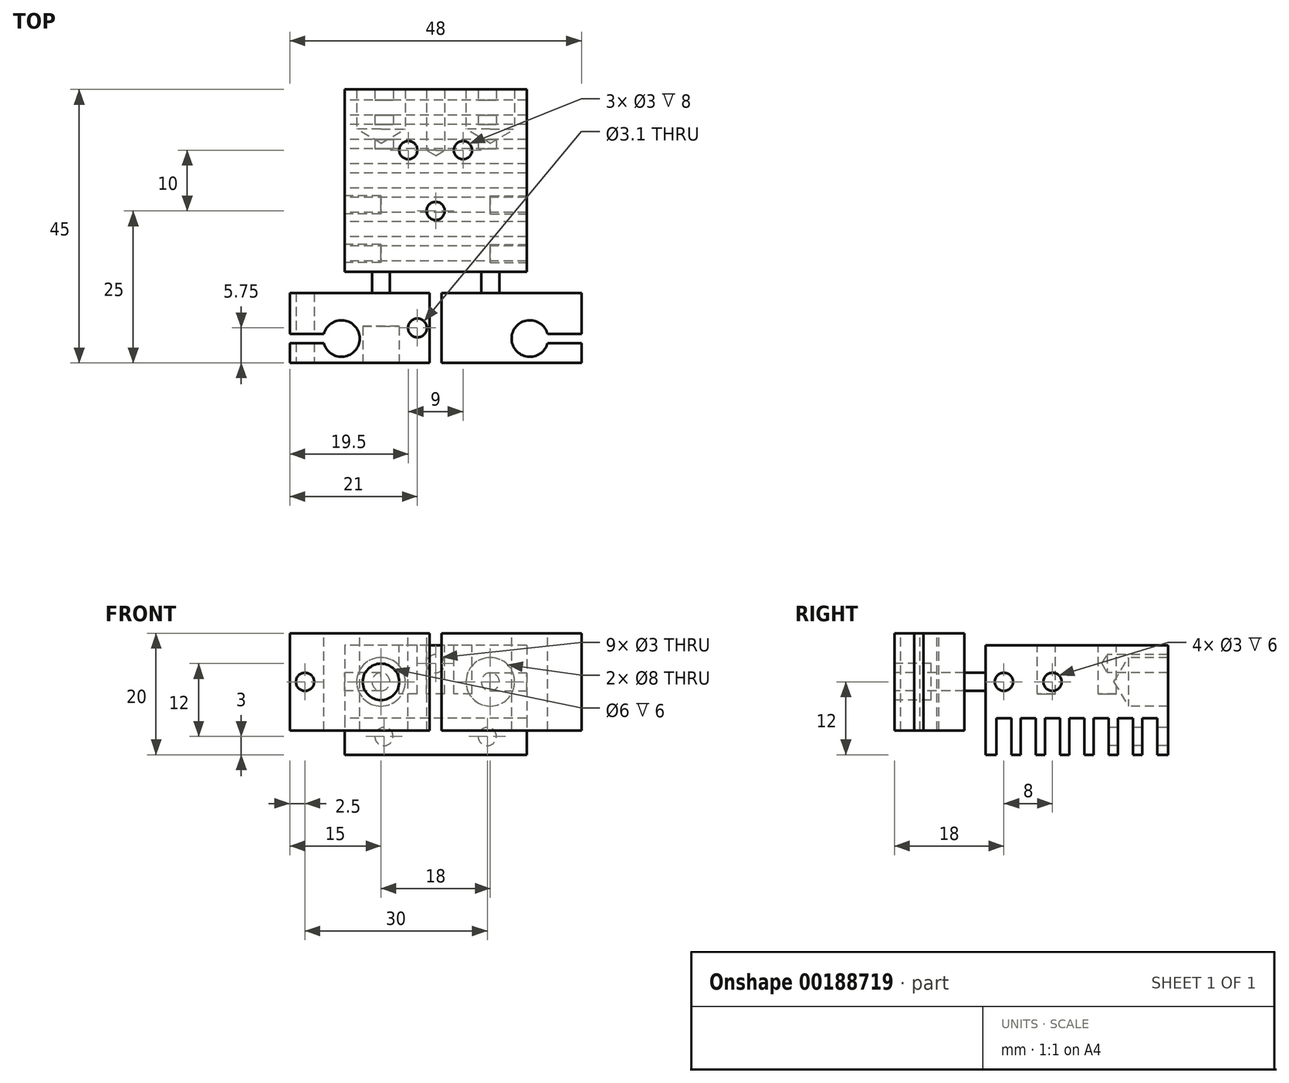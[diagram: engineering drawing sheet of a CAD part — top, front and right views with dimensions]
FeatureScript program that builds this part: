
annotation { "Feature Type Name" : "Feature", "Feature Type Description" : "" }
export const myFeature = defineFeature(function(context is Context, id is Id, definition is map)
    precondition{}
    {
        {
            var Q0;
            Q0=qCreatedBy(makeId("Top.planeOp"),FACE);
            var sketch = newSketch(context, id + "F0", { "sketchPlane" : qUnion([Q0])});
            skLineSegment(sketch, "E0.bottom", {"start": v(15, -15) * mm, "end": v(-15, -15) * mm});
            skLineSegment(sketch, "E0.top", {"start": v(15, 15) * mm, "end": v(-15, 15) * mm});
            skLineSegment(sketch, "E0.left", {"start": v(15, -15) * mm, "end": v(15, 15) * mm});
            skLineSegment(sketch, "E0.right", {"start": v(-15, -15) * mm, "end": v(-15, 15) * mm});
            skPoint(sketch, "E0.middle", {"position": v(0, 0) * mm});
            skSolve(sketch);
        }
        {
            var Q0;
            Q0=makeQuery(id+"F0.imprint","IMPRINT",FACE,{"disambiguationData":[TD([[makeQuery(id+"F0.imprint","IMPRINT",EDGE,{"derivedFrom":sQuery(id+"F0.wireOp",EDGE,"E0.bottom")}),-1.0]])]});
            extrude(context, id + "F15", {"entities" : qUnion([Q0]), "depth" : 18 * mm});
        }
        {
            var Q0;
            Q0=makeQuery(id+"F15.opExtrude","SWEPT_FACE",FACE,{"disambiguationData":[OSD([sQuery(id+"F0.wireOp",EDGE,"E0.top")])]});
            var sketch = newSketch(context, id + "F16", { "sketchPlane" : qUnion([Q0])});
            skPoint(sketch, "E1", {"position": v(-8.5, 3) * mm});
            skPoint(sketch, "E2", {"position": v(8.5, 3) * mm});
            skPoint(sketch, "E3", {"position": v(-9, 12) * mm});
            skPoint(sketch, "E4", {"position": v(9, 12) * mm});
            skPoint(sketch, "E5", {"position": v(0, 15) * mm});
            skSolve(sketch);
        }
        {
            var Q0;
            Q0=sQuery(id+"F16.wireOp",VERTEX,"E3");
            var Q1;
            Q1=sQuery(id+"F16.wireOp",VERTEX,"E4");
            var Q2;
            Q2=makeQuery(id+"F15.opExtrude","SWEPT_BODY",BODY,{"disambiguationData":[OSD([sQuery(id+"F0.wireOp",EDGE,"E0.bottom"),sQuery(id+"F0.wireOp",EDGE,"E0.top"),sQuery(id+"F0.wireOp",EDGE,"E0.left"),sQuery(id+"F0.wireOp",EDGE,"E0.right")])]});
            hole(context, id + "F1", {"style" : HoleStyle.SIMPLE, "endStyle" : HoleEndStyle.BLIND, "holeDiameter" : 8 * mm, "holeDepth" : 6.5 * mm, "locations" : qUnion([Q0, Q1]), "scope" : qUnion([Q2]), "tappedDepth" : 12 * mm, "tapClearance" : 3, "startStyle" : HoleStartStyle.PART});
        }
        {
            var Q0;
            Q0=makeQuery(id+"F15.opExtrude","CAP_FACE",FACE,{"disambiguationData":[OSD([sQuery(id+"F0.wireOp",EDGE,"E0.bottom"),sQuery(id+"F0.wireOp",EDGE,"E0.top"),sQuery(id+"F0.wireOp",EDGE,"E0.left"),sQuery(id+"F0.wireOp",EDGE,"E0.right")])],"isStart":true});
            var sketch = newSketch(context, id + "F17", { "sketchPlane" : qUnion([Q0])});
            skLineSegment(sketch, "E6.bottom", {"start": v(15, -13.25) * mm, "end": v(-15.01, -13.25) * mm});
            skLineSegment(sketch, "E6.top", {"start": v(15, -10.75) * mm, "end": v(-15.01, -10.75) * mm});
            skLineSegment(sketch, "E6.left", {"start": v(15, -13.25) * mm, "end": v(15, -10.75) * mm});
            skLineSegment(sketch, "E6.right", {"start": v(-15.01, -13.25) * mm, "end": v(-15.01, -10.75) * mm});
            skLineSegment(sketch, "E7.0.1.0", {"start": v(15, -9.25) * mm, "end": v(15, -6.75) * mm});
            skLineSegment(sketch, "E7.0.1.1", {"start": v(-15.01, -9.25) * mm, "end": v(-15.01, -6.75) * mm});
            skLineSegment(sketch, "E7.0.1.2", {"start": v(15, -9.25) * mm, "end": v(-15.01, -9.25) * mm});
            skLineSegment(sketch, "E7.0.1.3", {"start": v(15, -6.75) * mm, "end": v(-15.01, -6.75) * mm});
            skLineSegment(sketch, "E7.0.2.0", {"start": v(15, -5.25) * mm, "end": v(15, -2.75) * mm});
            skLineSegment(sketch, "E7.0.2.1", {"start": v(-15.01, -5.25) * mm, "end": v(-15.01, -2.75) * mm});
            skLineSegment(sketch, "E7.0.2.2", {"start": v(15, -5.25) * mm, "end": v(-15.01, -5.25) * mm});
            skLineSegment(sketch, "E7.0.2.3", {"start": v(15, -2.75) * mm, "end": v(-15.01, -2.75) * mm});
            skLineSegment(sketch, "E7.0.3.0", {"start": v(15, -1.25) * mm, "end": v(15, 1.25) * mm});
            skLineSegment(sketch, "E7.0.3.1", {"start": v(-15.01, -1.25) * mm, "end": v(-15.01, 1.25) * mm});
            skLineSegment(sketch, "E7.0.3.2", {"start": v(15, -1.25) * mm, "end": v(-15.01, -1.25) * mm});
            skLineSegment(sketch, "E7.0.3.3", {"start": v(15, 1.25) * mm, "end": v(-15.01, 1.25) * mm});
            skLineSegment(sketch, "E7.0.4.0", {"start": v(15, 2.75) * mm, "end": v(15, 5.25) * mm});
            skLineSegment(sketch, "E7.0.4.1", {"start": v(-15.01, 2.75) * mm, "end": v(-15.01, 5.25) * mm});
            skLineSegment(sketch, "E7.0.4.2", {"start": v(15, 2.75) * mm, "end": v(-15.01, 2.75) * mm});
            skLineSegment(sketch, "E7.0.4.3", {"start": v(15, 5.25) * mm, "end": v(-15.01, 5.25) * mm});
            skLineSegment(sketch, "E7.0.5.0", {"start": v(15, 6.75) * mm, "end": v(15, 9.25) * mm});
            skLineSegment(sketch, "E7.0.5.1", {"start": v(-15.01, 6.75) * mm, "end": v(-15.01, 9.25) * mm});
            skLineSegment(sketch, "E7.0.5.2", {"start": v(15, 6.75) * mm, "end": v(-15.01, 6.75) * mm});
            skLineSegment(sketch, "E7.0.5.3", {"start": v(15, 9.25) * mm, "end": v(-15.01, 9.25) * mm});
            skLineSegment(sketch, "E7.0.6.0", {"start": v(15, 10.75) * mm, "end": v(15, 13.25) * mm});
            skLineSegment(sketch, "E7.0.6.1", {"start": v(-15.01, 10.75) * mm, "end": v(-15.01, 13.25) * mm});
            skLineSegment(sketch, "E7.0.6.2", {"start": v(15, 10.75) * mm, "end": v(-15.01, 10.75) * mm});
            skLineSegment(sketch, "E7.0.6.3", {"start": v(15, 13.25) * mm, "end": v(-15.01, 13.25) * mm});
            skLineSegment(sketch, "E7.direction1", {"start": v(-15.01, -13.25) * mm, "end": v(9.99, -13.25) * mm, "construction": true});
            skLineSegment(sketch, "E7.direction2", {"start": v(-15.01, -13.25) * mm, "end": v(-15.01, -9.25) * mm, "construction": true});
            skSolve(sketch);
        }
        {
            var Q0;
            {var subQ0=sQuery(id+"F17.wireOp",EDGE,"E7.0.6.0");Q0=makeQuery(id+"F17.imprint","IMPRINT",FACE,{"disambiguationData":[TD([[makeQuery(id+"F17.imprint","IMPRINT",EDGE,{"derivedFrom":subQ0}),-1.0]])]});}
            var Q1;
            {var subQ0=sQuery(id+"F17.wireOp",EDGE,"E7.0.5.0");Q1=makeQuery(id+"F17.imprint","IMPRINT",FACE,{"disambiguationData":[TD([[makeQuery(id+"F17.imprint","IMPRINT",EDGE,{"derivedFrom":subQ0}),-1.0]])]});}
            var Q2;
            {var subQ0=sQuery(id+"F17.wireOp",EDGE,"E7.0.4.0");Q2=makeQuery(id+"F17.imprint","IMPRINT",FACE,{"disambiguationData":[TD([[makeQuery(id+"F17.imprint","IMPRINT",EDGE,{"derivedFrom":subQ0}),-1.0]])]});}
            var Q3;
            {var subQ0=sQuery(id+"F17.wireOp",EDGE,"E7.0.3.0");Q3=makeQuery(id+"F17.imprint","IMPRINT",FACE,{"disambiguationData":[TD([[makeQuery(id+"F17.imprint","IMPRINT",EDGE,{"derivedFrom":subQ0}),-1.0]])]});}
            var Q4;
            {var subQ0=sQuery(id+"F17.wireOp",EDGE,"E7.0.2.0");Q4=makeQuery(id+"F17.imprint","IMPRINT",FACE,{"disambiguationData":[TD([[makeQuery(id+"F17.imprint","IMPRINT",EDGE,{"derivedFrom":subQ0}),-1.0]])]});}
            var Q5;
            {var subQ0=sQuery(id+"F17.wireOp",EDGE,"E7.0.1.0");Q5=makeQuery(id+"F17.imprint","IMPRINT",FACE,{"disambiguationData":[TD([[makeQuery(id+"F17.imprint","IMPRINT",EDGE,{"derivedFrom":subQ0}),-1.0]])]});}
            var Q6;
            {var subQ0=sQuery(id+"F17.wireOp",EDGE,"E6.left");Q6=makeQuery(id+"F17.imprint","IMPRINT",FACE,{"disambiguationData":[TD([[makeQuery(id+"F17.imprint","IMPRINT",EDGE,{"derivedFrom":subQ0}),-1.0]])]});}
            extrude(context, id + "F18", {"entities" : qUnion([Q0, Q1, Q2, Q3, Q4, Q5, Q6]), "operationType" : NewBodyOperationType.REMOVE, "oppositeDirection" : true, "depth" : 6 * mm});
        }
        {
            var Q0;
            Q0=sQuery(id+"F16.wireOp",VERTEX,"E2");
            var Q1;
            Q1=sQuery(id+"F16.wireOp",VERTEX,"E1");
            var Q2;
            Q2=sQuery(id+"F16.wireOp",VERTEX,"E5");
            var Q3;
            Q3=makeQuery(id+"F15.opExtrude","SWEPT_BODY",BODY,{"disambiguationData":[OSD([sQuery(id+"F0.wireOp",EDGE,"E0.bottom"),sQuery(id+"F0.wireOp",EDGE,"E0.top"),sQuery(id+"F0.wireOp",EDGE,"E0.left"),sQuery(id+"F0.wireOp",EDGE,"E0.right")])]});
            hole(context, id + "F19", {"style" : HoleStyle.SIMPLE, "endStyle" : HoleEndStyle.BLIND, "holeDiameter" : 3 * mm, "holeDepth" : 10 * mm, "locations" : qUnion([Q0, Q1, Q2]), "scope" : qUnion([Q3]), "startStyle" : HoleStartStyle.PART});
        }
        {
            var Q0;
            Q0=makeQuery(id+"F15.opExtrude","SWEPT_FACE",FACE,{"disambiguationData":[OSD([sQuery(id+"F0.wireOp",EDGE,"E0.bottom")])]});
            var sketch = newSketch(context, id + "F2", { "sketchPlane" : qUnion([Q0])});
            skCircle(sketch, "E8", {"center": v(9, 12) * mm, "radius": 1.48 * mm});
            skCircle(sketch, "E9", {"center": v(-9, 12) * mm, "radius": 1.48 * mm});
            skLineSegment(sketch, "E10", {"start": v(-15, 12) * mm, "end": v(15, 12) * mm, "construction": true});
            skSolve(sketch);
        }
        {
            var Q0;
            Q0=makeQuery(id+"F2.imprint","IMPRINT",FACE,{"disambiguationData":[TD([[makeQuery(id+"F2.imprint","IMPRINT",EDGE,{"derivedFrom":sQuery(id+"F2.wireOp",EDGE,"E9")}),1.0]])]});
            var Q1;
            Q1=makeQuery(id+"F2.imprint","IMPRINT",FACE,{"disambiguationData":[TD([[makeQuery(id+"F2.imprint","IMPRINT",EDGE,{"derivedFrom":sQuery(id+"F2.wireOp",EDGE,"E8")}),1.0]])]});
            extrude(context, id + "F3", {"entities" : qUnion([Q0, Q1]), "operationType" : NewBodyOperationType.ADD, "depth" : 3.5 * mm});
        }
        {
            var Q0;
            Q0=makeQuery(id+"F3.opExtrude","CAP_FACE",FACE,{"disambiguationData":[OSD([sQuery(id+"F2.wireOp",EDGE,"E8")])],"isStart":false});
            cPlane(context, id + "F4", {"entities" : qUnion([Q0]), "cplaneType" : CPlaneType.OFFSET, "offset" : 0 * mm, "width" : 150 * mm, "height" : 150 * mm});
        }
        {
            var Q0;
            Q0=qCreatedBy(id+"F4.planeOp",FACE);
            var sketch = newSketch(context, id + "F20", { "sketchPlane" : qUnion([Q0])});
            skPoint(sketch, "E11", {"position": v(-9, 12) * mm});
            skLineSegment(sketch, "E12.bottom", {"start": v(-1, 20) * mm, "end": v(-1, 4) * mm});
            skLineSegment(sketch, "E12.top", {"start": v(-24, 20) * mm, "end": v(-24, 4) * mm});
            skLineSegment(sketch, "E12.left", {"start": v(-1, 20) * mm, "end": v(-24, 20) * mm});
            skLineSegment(sketch, "E12.right", {"start": v(-1, 4) * mm, "end": v(-24, 4) * mm});
            skLineSegment(sketch, "E13", {"start": v(-1, 12) * mm, "end": v(-24, 12) * mm, "construction": true});
            skCircle(sketch, "E14.0", {"center": v(-9, 12) * mm, "radius": 1.48 * mm, "construction": true});
            skLineSegment(sketch, "E15", {"start": v(0, 0) * mm, "end": v(0, 25.96) * mm, "construction": true});
            skLineSegment(sketch, "E16.MirrorCS", {"start": v(1, 12) * mm, "end": v(24, 12) * mm, "construction": true});
            skLineSegment(sketch, "E17.MirrorCS", {"start": v(24, 20) * mm, "end": v(24, 4) * mm});
            skLineSegment(sketch, "E18.MirrorCS", {"start": v(1, 4) * mm, "end": v(24, 4) * mm});
            skLineSegment(sketch, "E19.MirrorCS", {"start": v(1, 20) * mm, "end": v(1, 4) * mm});
            skCircle(sketch, "E20.MirrorC", {"center": v(9, 12) * mm, "radius": 1.48 * mm, "construction": true});
            skLineSegment(sketch, "E21.MirrorCS", {"start": v(1, 20) * mm, "end": v(24, 20) * mm});
            skSolve(sketch);
        }
        {
            var Q0;
            Q0=makeQuery(id+"F20.imprint","IMPRINT",FACE,{"disambiguationData":[TD([[makeQuery(id+"F20.imprint","IMPRINT",EDGE,{"derivedFrom":sQuery(id+"F20.wireOp",EDGE,"E12.bottom")}),-1.0]])]});
            var Q1;
            Q1=makeQuery(id+"F20.imprint","IMPRINT",FACE,{"disambiguationData":[TD([[makeQuery(id+"F20.imprint","IMPRINT",EDGE,{"derivedFrom":sQuery(id+"F20.wireOp",EDGE,"E17.MirrorCS")}),-1.0]])]});
            extrude(context, id + "F21", {"entities" : qUnion([Q0, Q1]), "operationType" : NewBodyOperationType.ADD, "depth" : 11.5 * mm, "offsetDistance" : 25 * mm});
        }
        {
            var Q0;
            Q0=makeQuery(id+"F21.opExtrude","CAP_FACE",FACE,{"disambiguationData":[OSD([sQuery(id+"F20.wireOp",EDGE,"E12.bottom"),sQuery(id+"F20.wireOp",EDGE,"E12.top"),sQuery(id+"F20.wireOp",EDGE,"E12.left"),sQuery(id+"F20.wireOp",EDGE,"E12.right")])],"isStart":false});
            var sketch = newSketch(context, id + "F22", { "sketchPlane" : qUnion([Q0])});
            skCircle(sketch, "E22", {"center": v(-9, 12) * mm, "radius": 3 * mm});
            skCircle(sketch, "E23", {"center": v(-21.5, 12) * mm, "radius": 1.5 * mm});
            skLineSegment(sketch, "E24", {"start": v(0, 0) * mm, "end": v(0, 26.65) * mm, "construction": true});
            skCircle(sketch, "E25.MirrorC", {"center": v(21.5, 12) * mm, "radius": 1.5 * mm});
            skCircle(sketch, "E26.MirrorC", {"center": v(9, 12) * mm, "radius": 3 * mm});
            skSolve(sketch);
        }
        {
            var Q0;
            Q0=makeQuery(id+"F22.imprint","IMPRINT",FACE,{"disambiguationData":[TD([[makeQuery(id+"F22.imprint","IMPRINT",EDGE,{"derivedFrom":sQuery(id+"F22.wireOp",EDGE,"E22")}),1.0]])]});
            var Q1;
            Q1=makeQuery(id+"F22.imprint","IMPRINT",FACE,{"disambiguationData":[TD([[makeQuery(id+"F22.imprint","IMPRINT",EDGE,{"derivedFrom":sQuery(id+"F22.wireOp",EDGE,"E26.MirrorC")}),-1.0]])]});
            extrude(context, id + "F5", {"entities" : qUnion([Q0, Q1]), "operationType" : NewBodyOperationType.REMOVE, "oppositeDirection" : true, "depth" : 6 * mm, "offsetDistance" : 25 * mm});
        }
        {
            var Q0;
            Q0=makeQuery(id+"F22.imprint","IMPRINT",FACE,{"disambiguationData":[TD([[makeQuery(id+"F22.imprint","IMPRINT",EDGE,{"derivedFrom":sQuery(id+"F22.wireOp",EDGE,"E23")}),1.0]])]});
            var Q1;
            Q1=makeQuery(id+"F22.imprint","IMPRINT",FACE,{"disambiguationData":[TD([[makeQuery(id+"F22.imprint","IMPRINT",EDGE,{"derivedFrom":sQuery(id+"F22.wireOp",EDGE,"E25.MirrorC")}),-1.0]])]});
            extrude(context, id + "F6", {"entities" : qUnion([Q0, Q1]), "operationType" : NewBodyOperationType.REMOVE, "endBound" : BoundingType.UP_TO_NEXT, "oppositeDirection" : true, "depth" : 25 * mm, "offsetDistance" : 25 * mm});
        }
        {
            var Q0;
            Q0=makeQuery(id+"F21.opExtrude","SWEPT_FACE",FACE,{"disambiguationData":[OSD([sQuery(id+"F20.wireOp",EDGE,"E12.left")])]});
            var sketch = newSketch(context, id + "F7", { "sketchPlane" : qUnion([Q0])});
            skArc(sketch, "E27", {"start": v(-18.4, -26.75) * mm, "mid": v(-12.5, -26) * mm, "end": v(-18.4, -25.25) * mm});
            skLineSegment(sketch, "E28.bottom", {"start": v(-24, -26.75) * mm, "end": v(-24, -25.25) * mm});
            skLineSegment(sketch, "E28.left", {"start": v(-24, -26.75) * mm, "end": v(-18.4, -26.75) * mm});
            skLineSegment(sketch, "E28.right", {"start": v(-24, -25.25) * mm, "end": v(-18.4, -25.25) * mm});
            skLineSegment(sketch, "E29", {"start": v(-15.5, -26) * mm, "end": v(-24, -26) * mm, "construction": true});
            skCircle(sketch, "E30", {"center": v(-3, -24.25) * mm, "radius": 1.55 * mm});
            skLineSegment(sketch, "E31", {"start": v(0, -30.03) * mm, "end": v(0, -16.1) * mm, "construction": true});
            skLineSegment(sketch, "E32.MirrorCS", {"start": v(24, -26.75) * mm, "end": v(24, -25.25) * mm});
            skPoint(sketch, "E33.MirrorP", {"position": v(15.5, -26) * mm});
            skCircle(sketch, "E34.MirrorC", {"center": v(3, -24.25) * mm, "radius": 1.55 * mm});
            skLineSegment(sketch, "E35.MirrorCS", {"start": v(24, -26.75) * mm, "end": v(18.4, -26.75) * mm});
            skLineSegment(sketch, "E36.MirrorCS", {"start": v(15.5, -26) * mm, "end": v(24, -26) * mm, "construction": true});
            skLineSegment(sketch, "E37.MirrorCS", {"start": v(24, -25.25) * mm, "end": v(18.4, -25.25) * mm});
            skArc(sketch, "E38.MirrorCS", {"start": v(18.4, -26.75) * mm, "mid": v(12.5, -26) * mm, "end": v(18.4, -25.25) * mm});
            skSolve(sketch);
        }
        {
            var Q0;
            Q0=makeQuery(id+"F7.imprint","IMPRINT",FACE,{"disambiguationData":[TD([[makeQuery(id+"F7.imprint","IMPRINT",EDGE,{"derivedFrom":sQuery(id+"F7.wireOp",EDGE,"E27")}),1.0]])]});
            var Q1;
            Q1=makeQuery(id+"F7.imprint","IMPRINT",FACE,{"disambiguationData":[TD([[makeQuery(id+"F7.imprint","IMPRINT",EDGE,{"derivedFrom":sQuery(id+"F7.wireOp",EDGE,"E30")}),1.0]])]});
            var Q2;
            Q2=makeQuery(id+"F7.imprint","IMPRINT",FACE,{"disambiguationData":[TD([[makeQuery(id+"F7.imprint","IMPRINT",EDGE,{"derivedFrom":sQuery(id+"F7.wireOp",EDGE,"E34.MirrorC")}),-1.0]])]});
            var Q3;
            Q3=makeQuery(id+"F7.imprint","IMPRINT",FACE,{"disambiguationData":[TD([[makeQuery(id+"F7.imprint","IMPRINT",EDGE,{"derivedFrom":sQuery(id+"F7.wireOp",EDGE,"E32.MirrorCS")}),1.0]])]});
            var Q4;
            Q4=makeQuery(id+"F21.opExtrude","SWEPT_FACE",FACE,{"disambiguationData":[OSD([sQuery(id+"F20.wireOp",EDGE,"E12.right")])]});
            extrude(context, id + "F23", {"entities" : qUnion([Q0, Q1, Q2, Q3]), "operationType" : NewBodyOperationType.REMOVE, "endBound" : BoundingType.UP_TO_SURFACE, "oppositeDirection" : true, "endBoundEntityFace" : qUnion([Q4]), "depth" : 25 * mm, "offsetDistance" : 25 * mm});
        }
        {
            var Q0;
            Q0=makeQuery(id+"F15.opExtrude","CAP_FACE",FACE,{"disambiguationData":[OSD([sQuery(id+"F0.wireOp",EDGE,"E0.bottom"),sQuery(id+"F0.wireOp",EDGE,"E0.top"),sQuery(id+"F0.wireOp",EDGE,"E0.left"),sQuery(id+"F0.wireOp",EDGE,"E0.right")])],"isStart":false});
            var sketch = newSketch(context, id + "F8", { "sketchPlane" : qUnion([Q0])});
            skLineSegment(sketch, "E39", {"start": v(-15, -12) * mm, "end": v(15, -12) * mm, "construction": true});
            skLineSegment(sketch, "E40", {"start": v(-15, -4) * mm, "end": v(15, -4) * mm, "construction": true});
            skLineSegment(sketch, "E41", {"start": v(-15, 5) * mm, "end": v(15, 5) * mm, "construction": true});
            skLineSegment(sketch, "E42", {"start": v(-15, -5) * mm, "end": v(15, -5) * mm, "construction": true});
            skLineSegment(sketch, "E43", {"start": v(0, -15) * mm, "end": v(0, 15) * mm, "construction": true});
            skCircle(sketch, "E44", {"center": v(0, -5) * mm, "radius": 1.5 * mm});
            skCircle(sketch, "E45", {"center": v(-4.5, 5) * mm, "radius": 1.5 * mm});
            skCircle(sketch, "E46", {"center": v(4.5, 5) * mm, "radius": 1.5 * mm});
            skSolve(sketch);
        }
        {
            var Q0;
            Q0=makeQuery(id+"F8.imprint","IMPRINT",FACE,{"disambiguationData":[TD([[makeQuery(id+"F8.imprint","IMPRINT",EDGE,{"derivedFrom":sQuery(id+"F8.wireOp",EDGE,"ywnUtpi9-7H2P-GrDI-hZVL-qsXkbOsszN2Q")}),1.0]])]});
            var Q1;
            Q1=makeQuery(id+"F8.imprint","IMPRINT",FACE,{"disambiguationData":[TD([[makeQuery(id+"F8.imprint","IMPRINT",EDGE,{"derivedFrom":sQuery(id+"F8.wireOp",EDGE,"L3KA2nMo-dCnA-nJDB-VwEg-LmUIuubpB5nK")}),1.0]])]});
            var Q2;
            Q2=makeQuery(id+"F8.imprint","IMPRINT",FACE,{"disambiguationData":[TD([[makeQuery(id+"F8.imprint","IMPRINT",EDGE,{"derivedFrom":sQuery(id+"F8.wireOp",EDGE,"E44")}),1.0]])]});
            var Q3;
            Q3=makeQuery(id+"F8.imprint","IMPRINT",FACE,{"disambiguationData":[TD([[makeQuery(id+"F8.imprint","IMPRINT",EDGE,{"derivedFrom":sQuery(id+"F8.wireOp",EDGE,"E46")}),1.0]])]});
            var Q4;
            Q4=makeQuery(id+"F8.imprint","IMPRINT",FACE,{"disambiguationData":[TD([[makeQuery(id+"F8.imprint","IMPRINT",EDGE,{"derivedFrom":sQuery(id+"F8.wireOp",EDGE,"E1vzGFQg-AsZZ-Da02-JAcT-oJih4ZFW7Igx")}),1.0]])]});
            var Q5;
            Q5=makeQuery(id+"F8.imprint","IMPRINT",FACE,{"disambiguationData":[TD([[makeQuery(id+"F8.imprint","IMPRINT",EDGE,{"derivedFrom":sQuery(id+"F8.wireOp",EDGE,"YLegpueE-Kfmy-qUzq-qPqj-2WKwct9rmbxn")}),1.0]])]});
            var Q6;
            Q6=makeQuery(id+"F8.imprint","IMPRINT",FACE,{"disambiguationData":[TD([[makeQuery(id+"F8.imprint","IMPRINT",EDGE,{"derivedFrom":sQuery(id+"F8.wireOp",EDGE,"E45")}),1.0]])]});
            extrude(context, id + "F9", {"entities" : qUnion([Q0, Q1, Q2, Q3, Q4, Q5, Q6]), "operationType" : NewBodyOperationType.REMOVE, "oppositeDirection" : true, "depth" : 8 * mm});
        }
        {
            var Q0;
            Q0=makeQuery(id+"F22.imprint","IMPRINT",FACE,{"disambiguationData":[TD([[makeQuery(id+"F22.imprint","IMPRINT",EDGE,{"derivedFrom":sQuery(id+"F22.wireOp",EDGE,"E22")}),1.0]])]});
            var Q1;
            Q1=makeQuery(id+"F22.imprint","IMPRINT",FACE,{"disambiguationData":[TD([[makeQuery(id+"F22.imprint","IMPRINT",EDGE,{"derivedFrom":sQuery(id+"F22.wireOp",EDGE,"3IGajT9g-2yW0-HcNw-kY0E-KYSIm1LMgEkU")}),1.0]])]});
            extrude(context, id + "F10", {"entities" : qUnion([Q0, Q1]), "operationType" : NewBodyOperationType.REMOVE, "oppositeDirection" : true, "depth" : 6 * mm, "offsetDistance" : 25 * mm});
        }
        {
            var Q0;
            Q0=makeQuery(id+"F15.opExtrude","SWEPT_FACE",FACE,{"disambiguationData":[OSD([sQuery(id+"F0.wireOp",EDGE,"E0.left")])]});
            var sketch = newSketch(context, id + "F11", { "sketchPlane" : qUnion([Q0])});
            skLineSegment(sketch, "E47", {"start": v(-15, 12) * mm, "end": v(15, 12) * mm, "construction": true});
            skCircle(sketch, "E48", {"center": v(-12, 12) * mm, "radius": 1.5 * mm});
            skCircle(sketch, "E49", {"center": v(-4, 12) * mm, "radius": 1.5 * mm});
            skSolve(sketch);
        }
        {
            var Q0;
            Q0=makeQuery(id+"F11.imprint","IMPRINT",FACE,{"disambiguationData":[TD([[makeQuery(id+"F11.imprint","IMPRINT",EDGE,{"derivedFrom":sQuery(id+"F11.wireOp",EDGE,"E48")}),1.0]])]});
            var Q1;
            Q1=makeQuery(id+"F11.imprint","IMPRINT",FACE,{"disambiguationData":[TD([[makeQuery(id+"F11.imprint","IMPRINT",EDGE,{"derivedFrom":sQuery(id+"F11.wireOp",EDGE,"E49")}),1.0]])]});
            extrude(context, id + "F12", {"entities" : qUnion([Q0, Q1]), "oppositeDirection" : true, "depth" : 6 * mm, "offsetDistance" : 25 * mm});
        }
        {
            var Q0;
            Q0=makeQuery(id+"F12.opExtrude","SWEPT_BODY",BODY,{"disambiguationData":[OSD([sQuery(id+"F11.wireOp",EDGE,"E49")])]});
            var Q1;
            Q1=makeQuery(id+"F12.opExtrude","SWEPT_BODY",BODY,{"disambiguationData":[OSD([sQuery(id+"F11.wireOp",EDGE,"E48")])]});
            var Q2;
            Q2=qCreatedBy(makeId("Right.planeOp"),FACE);
            mirror(context, id + "F13", {"operationType" : NewBodyOperationType.REMOVE, "entities" : qUnion([Q0, Q1]), "mirrorPlane" : qUnion([Q2])});
        }
        {
            var Q0;
            Q0=makeQuery(id+"F12.opExtrude","SWEPT_BODY",BODY,{"disambiguationData":[OSD([sQuery(id+"F11.wireOp",EDGE,"E48")])]});
            var Q1;
            Q1=makeQuery(id+"F12.opExtrude","SWEPT_BODY",BODY,{"disambiguationData":[OSD([sQuery(id+"F11.wireOp",EDGE,"E49")])]});
            var Q2;
            Q2=makeQuery(id+"F15.opExtrude","SWEPT_BODY",BODY,{"disambiguationData":[OSD([sQuery(id+"F0.wireOp",EDGE,"E0.bottom"),sQuery(id+"F0.wireOp",EDGE,"E0.top"),sQuery(id+"F0.wireOp",EDGE,"E0.left"),sQuery(id+"F0.wireOp",EDGE,"E0.right")])]});
            booleanBodies(context, id + "F14", {"operationType" : BooleanOperationType.SUBTRACTION, "tools" : qUnion([Q0, Q1]), "targets" : qUnion([Q2])});
        }
    });
